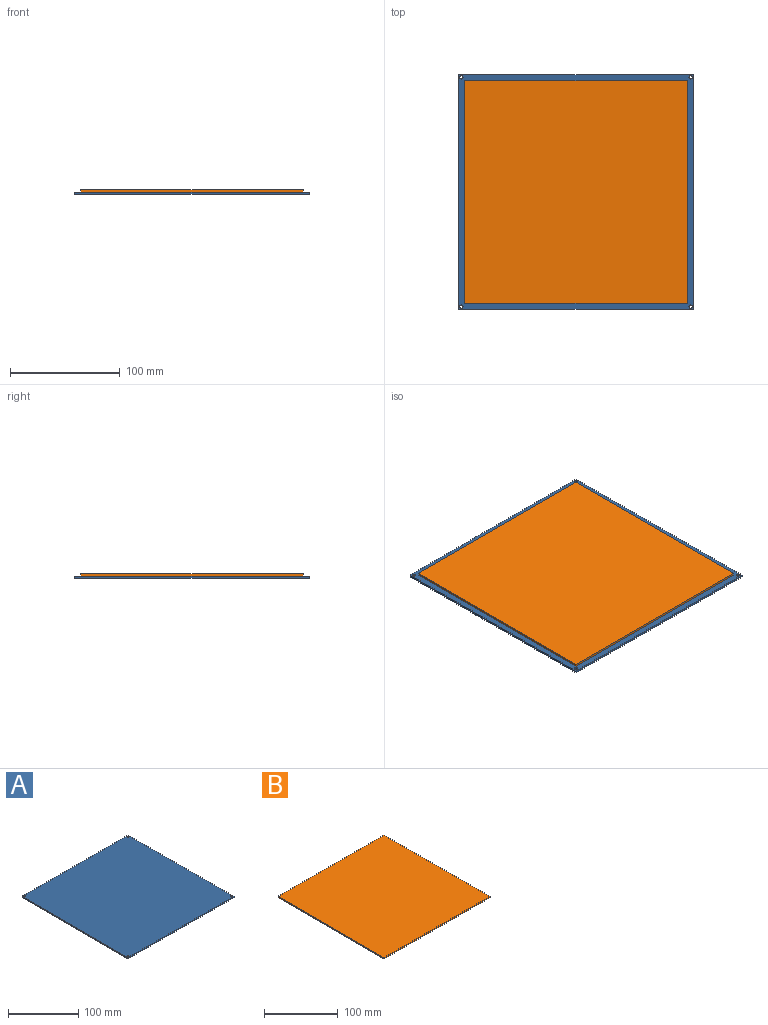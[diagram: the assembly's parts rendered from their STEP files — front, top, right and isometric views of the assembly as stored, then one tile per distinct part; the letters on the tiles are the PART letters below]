
ASSEMBLY  parts=2 mates=1
PART A: 10 faces, bbox 214x214x2 mm
  f0: plane 214x2mm, normal (0,-1,0), area 428mm2, adj f1,f3,f4,f5
  f1: plane 214x2mm, normal (1,0,0), area 428mm2, adj f0,f2,f4,f5
  f2: plane 214x2mm, normal (0,1,0), area 428mm2, adj f1,f3,f4,f5
  f3: plane 214x2mm, normal (-1,0,0), area 428mm2, adj f0,f2,f4,f5
  f4: plane 214x214mm, normal (0,0,1), area 45767.7mm2, adj f0,f1,f2,f3,f6,f7,f8,f9
  f5: plane 214x214mm, normal (0,0,-1), area 45767.7mm2, adj f0,f1,f2,f3,f6,f7,f8,f9
  f6: cylinder r=1.5mm len=3mm, axis (0,0,1), area 18.8mm2, adj f4,f5
  f7: cylinder r=1.5mm len=3mm, axis (0,0,1), area 18.8mm2, adj f4,f5
  f8: cylinder r=1.5mm len=3mm, axis (0,0,1), area 18.8mm2, adj f4,f5
  f9: cylinder r=1.5mm len=3mm, axis (0,0,1), area 18.8mm2, adj f4,f5
PART B: 6 faces, bbox 203x203x2 mm
  f0: plane 203x2mm, normal (0,-1,0), area 406mm2, adj f1,f3,f4,f5
  f1: plane 203x2mm, normal (1,0,0), area 406mm2, adj f0,f2,f4,f5
  f2: plane 203x2mm, normal (0,1,0), area 406mm2, adj f1,f3,f4,f5
  f3: plane 203x2mm, normal (-1,0,0), area 406mm2, adj f0,f2,f4,f5
  f4: plane 203x203mm, normal (0,0,1), area 41209mm2, adj f0,f1,f2,f3
  f5: plane 203x203mm, normal (0,0,-1), area 41209mm2, adj f0,f1,f2,f3
PLACE A t=(0,0,-26)mm
PLACE B t=(0,0,-26)mm
MATE fastened B.f5 <-> A.f4  axis (0,0,-1) through (0,0,2)mm
